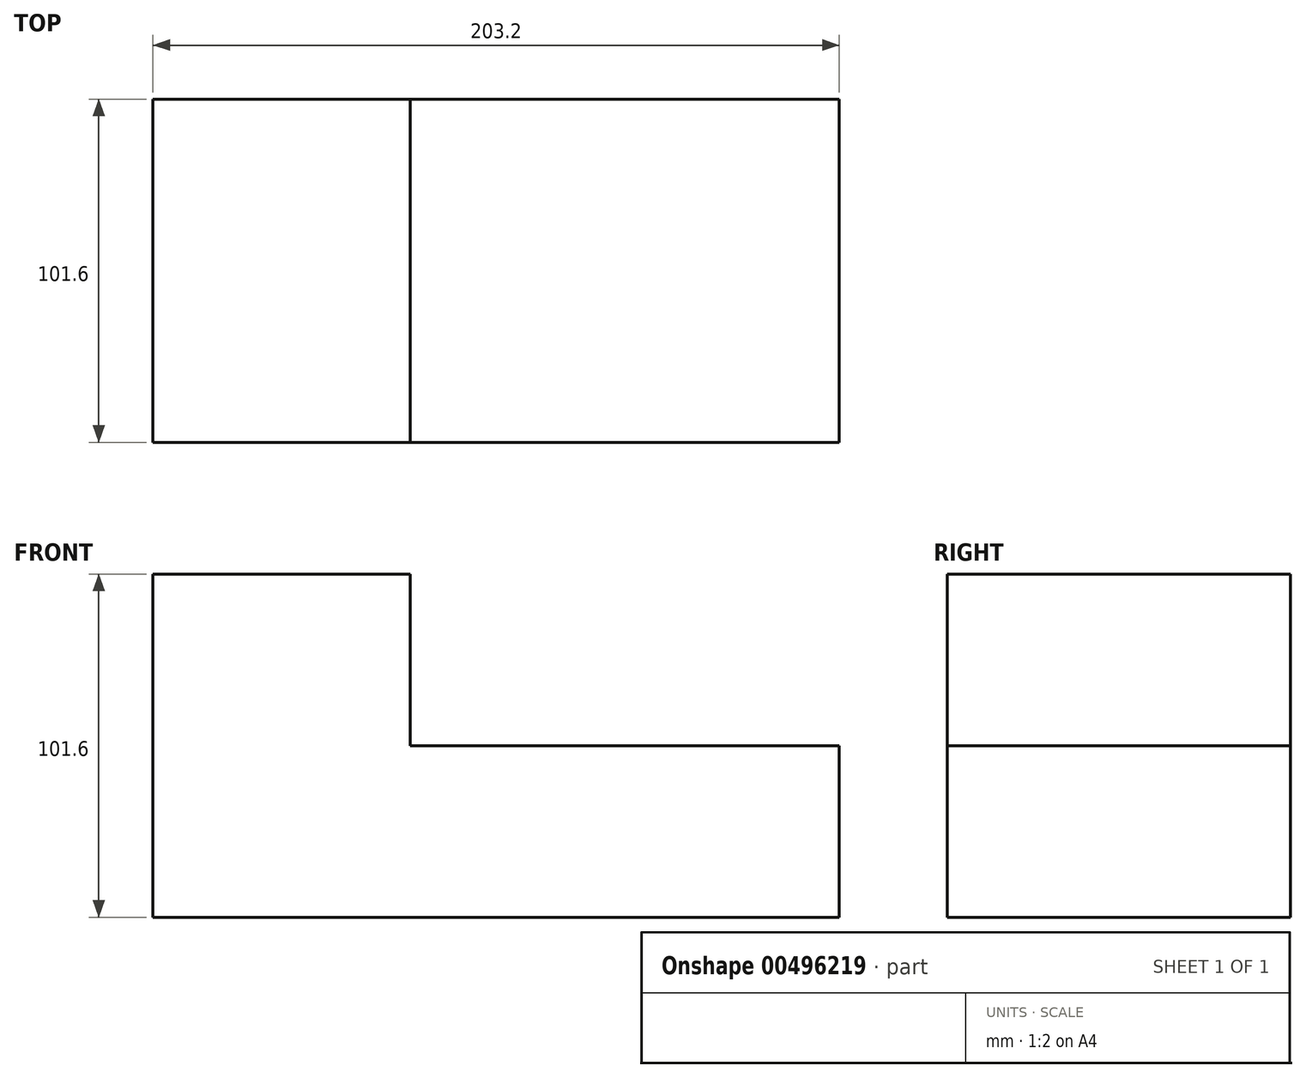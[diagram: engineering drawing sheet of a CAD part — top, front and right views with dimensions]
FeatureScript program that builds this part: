
annotation { "Feature Type Name" : "Feature", "Feature Type Description" : "" }
export const myFeature = defineFeature(function(context is Context, id is Id, definition is map)
    precondition{}
    {
        {
            var Q0;
            Q0=qCreatedBy(makeId("Top.planeOp"),FACE);
            var sketch = newSketch(context, id + "F0", { "sketchPlane" : qUnion([Q0])});
            skLineSegment(sketch, "E0.bottom", {"start": v(-74.53, 0) * mm, "end": v(128.67, 0) * mm});
            skLineSegment(sketch, "E0.top", {"start": v(-74.53, 101.6) * mm, "end": v(128.67, 101.6) * mm});
            skLineSegment(sketch, "E0.left", {"start": v(-74.53, 0) * mm, "end": v(-74.53, 101.6) * mm});
            skLineSegment(sketch, "E0.right", {"start": v(128.67, 0) * mm, "end": v(128.67, 101.6) * mm});
            skSolve(sketch);
        }
        {
            var Q0;
            Q0 = qSketchRegion(id + "F0", true);
            var Q1;
            Q1=makeQuery(id+"F0.imprint","IMPRINT",FACE,{"disambiguationData":[TD([[makeQuery(id+"F0.imprint","IMPRINT",EDGE,{"derivedFrom":sQuery(id+"F0.wireOp",EDGE,"E0.bottom")}),1.0]])]});
            extrude(context, id + "F1", {"entities" : qUnion([Q0, Q1]), "depth" : 101.6 * mm});
        }
        {
            var Q0;
            Q0=makeQuery(id+"F1.opExtrude","SWEPT_FACE",FACE,{"disambiguationData":[OSD([sQuery(id+"F0.wireOp",EDGE,"E0.bottom")])]});
            var sketch = newSketch(context, id + "F2", { "sketchPlane" : qUnion([Q0])});
            skLineSegment(sketch, "E1.bottom", {"start": v(1.67, 101.6) * mm, "end": v(128.67, 101.6) * mm});
            skLineSegment(sketch, "E1.top", {"start": v(1.67, 50.8) * mm, "end": v(128.67, 50.8) * mm});
            skLineSegment(sketch, "E1.left", {"start": v(1.67, 101.6) * mm, "end": v(1.67, 50.8) * mm});
            skLineSegment(sketch, "E1.right", {"start": v(128.67, 101.6) * mm, "end": v(128.67, 50.8) * mm});
            skSolve(sketch);
        }
        {
            var Q0;
            Q0 = qSketchRegion(id + "F2", true);
            extrude(context, id + "F3", {"entities" : qUnion([Q0]), "operationType" : NewBodyOperationType.REMOVE, "endBound" : BoundingType.UP_TO_NEXT, "oppositeDirection" : true, "depth" : 25.4 * mm});
        }
    });
